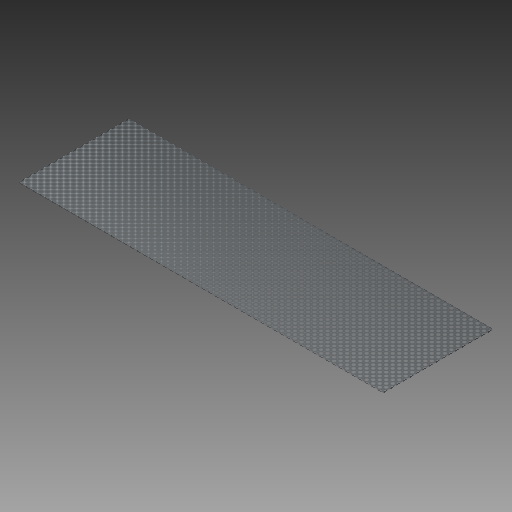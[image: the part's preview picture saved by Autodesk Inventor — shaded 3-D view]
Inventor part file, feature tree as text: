
AUTODESK INVENTOR PART (.ipt)
format: ipt  version: 2018 (Build 220112000, 112)  size: 144,896 bytes
history: native  units: mm
features: extrude x1
ambient origin geometry x8: Origin, YZ Plane, XZ Plane, XY Plane, X Axis, Y Axis, Z Axis, Center Point
bodies: Volumenkörper1 (feature_tree)
feature tree (1):
  extrude  "Extrusion1"  Depth=298.0mm
